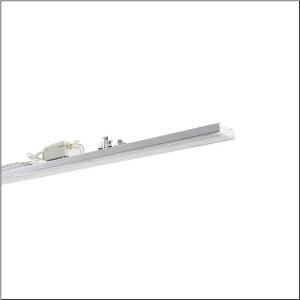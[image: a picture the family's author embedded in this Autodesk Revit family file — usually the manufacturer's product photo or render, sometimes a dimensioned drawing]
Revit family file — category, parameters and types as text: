
# Revit family: licross_21_recessed_ho_52te1edv4l2s
name_source: partatom
category: Lighting Fixtures
units: mm (PartAtom-declared; Revit-internal decimal feet)

## family parameters
Cut with Voids When Loaded = No
Host = Face
Light Source = No
Part Type = Normal
Room Calculation Point = No
Round Connector Dimension = Use Diameter
Shared = No

## types (1)
- --- (1 x LED, 22130 lm, 125.6 W, 4000K)
    Apparent Load = 126 VA
    CIE Flux Codes = 85 95 99 100 100
    Color Rendering = 80
    Color Temperature = 4000K
    Default Elevation = 1800 mm
    Description = Licross 21 Recessed HO, luminaire insert, of sheet steel, galvanised, coil coated, white, length: 2.250mm, width: 66mm, height: 67mm, LED rated luminous flux: 22.130lm, light colour: 840, SDCM (Standard Deviation of Colour Matching)MacAdam ≤ 3 SDCM (initial), control gear: DALI 2, with plug, 5-pole, with phase selection, mains connection: 220..240V, AC, 50/60Hz, rated input power: 126W, internal wiring halogen-free, primary light control with lens, of plastic, primary optical cover: cover, of PMMA, light emission: direct distribution, primary light characteristic: symmetric, protection rating (complete): IP54, insulation class (complete): insulation class I (protective earthing), certification: CE, ENEC, VDE, UKCA, protection symbol: D if used in an environment with non-conductive dust loads with corresponding accessories, impact resistance: IK06, permissible ambient temperature for indoor applications: -40..+30°C, corresponds to IFS (International Featured Standards) requirements for safety and quality in the food industry, reducing of maximum allowable ambient temperature of 5°C with ceiling mounting, LABS conformity tested according to VDMA 24364:2018-05, The light source and the operating device comply with the requirements of the Ecodesign Regulation (EU) 2019/2020 and are replaceable in accordance with this regulation, packaging unit: 1 piece
    Height = 58 mm
    Lamp = 1 x LED
    Lamp Light Flux = 22130 lm
    Lamp Power = 125.6 W
    Lamp count = 1
    Length = 2250 mm
    Luminous efficacy = 176 lm/W
    Manufacturer = Siteco
    ModVariant = No
    Model = 52TE1EDV4L2S
    Mounting Place = Ceiling
    Mounting Type = Pendant
    Number of Poles = 1
    OnlyDefault = Yes
    Power Factor = 1
    Product Name = Licross 21 Recessed HO
    Product group = luminaire insert | ceiling pendant
    ProductGroupID = 901
    Protection Class = Protection class I
    Protection Degree = IP 54
    RLX_Detail_Level = 1
    RLX_Emergency_Light_Flux = 0 lm
    RLX_Emergency_Type = 0
    RLX_Emergency_Type_DB = No
    RlxData = <blob elided: 30029 chars, md5=e4fd5831>
    Socket = socket
    Standby Power = 0 W
    System Light Flux = 22129 lm
    System Power = 126 W
    Type Comments = factory setting: luminous flux: 100 % | dim-lin: 254 | 489 mA
    Type Image = l_1296930.jpg
    URL = http://relux.com
    VarID = @adj_127145
    Voltage = 0 V
    Weight = 0.00 kg
    Width = 66 mm

## geometry (parser evidence)
native form markers: Blend x4, Sweep x8
no freeform markers — native parametric forms only
